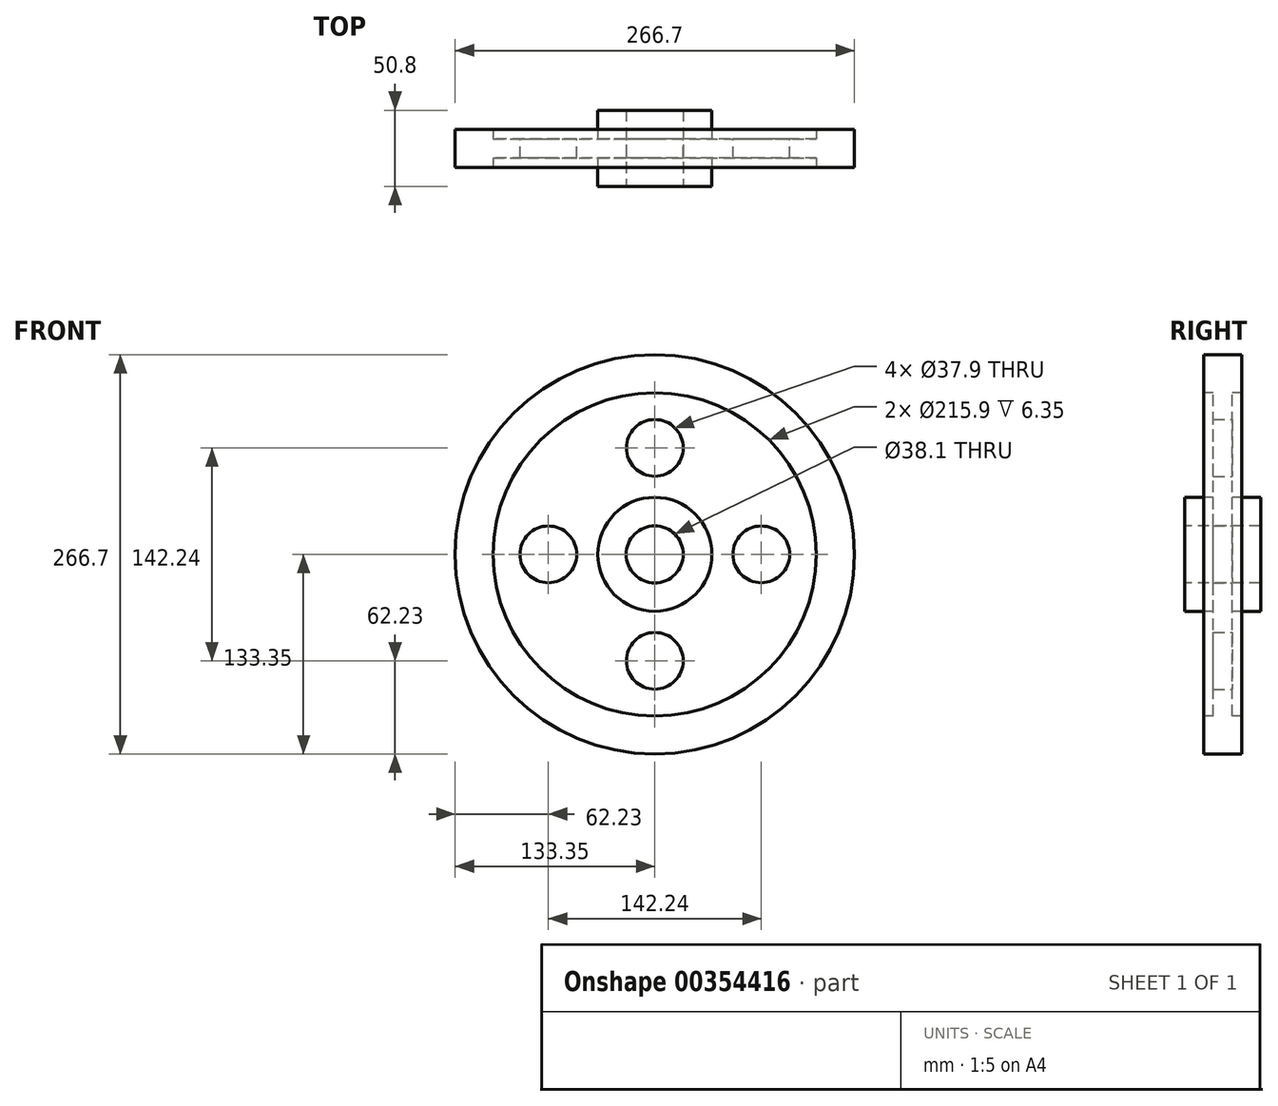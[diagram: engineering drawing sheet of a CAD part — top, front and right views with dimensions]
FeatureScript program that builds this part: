
annotation { "Feature Type Name" : "Feature", "Feature Type Description" : "" }
export const myFeature = defineFeature(function(context is Context, id is Id, definition is map)
    precondition{}
    {
        {
            var Q0;
            Q0=qCreatedBy(makeId("Right.planeOp"),FACE);
            var sketch = newSketch(context, id + "F0", { "sketchPlane" : qUnion([Q0])});
            skLineSegment(sketch, "E0", {"start": v(0, 0) * mm, "end": v(0, 28.58) * mm});
            skLineSegment(sketch, "E1", {"start": v(0, 28.58) * mm, "end": v(0, 73.03) * mm});
            skLineSegment(sketch, "E2", {"start": v(0, 73.03) * mm, "end": v(0, 120.65) * mm});
            skLineSegment(sketch, "E3.bottom", {"start": v(25.4, 19.05) * mm, "end": v(-25.4, 19.05) * mm});
            skLineSegment(sketch, "E3.top", {"start": v(25.4, 38.1) * mm, "end": v(6.35, 38.1) * mm});
            skLineSegment(sketch, "E3.left", {"start": v(25.4, 19.05) * mm, "end": v(25.4, 38.1) * mm});
            skLineSegment(sketch, "E3.right", {"start": v(-25.4, 19.05) * mm, "end": v(-25.4, 38.1) * mm});
            skPoint(sketch, "E3.middle", {"position": v(0, 28.58) * mm});
            skLineSegment(sketch, "E4.bottom", {"start": v(12.7, 107.95) * mm, "end": v(6.35, 107.95) * mm});
            skLineSegment(sketch, "E4.left", {"start": v(12.7, 107.95) * mm, "end": v(12.7, 133.35) * mm});
            skLineSegment(sketch, "E4.right", {"start": v(-12.7, 107.95) * mm, "end": v(-12.7, 133.35) * mm});
            skPoint(sketch, "E4.middle", {"position": v(0, 120.65) * mm});
            skLineSegment(sketch, "E5.top", {"start": v(0, 113.04) * mm, "end": v(-6.35, 113.04) * mm});
            skLineSegment(sketch, "E5.left", {"start": v(6.35, 33.01) * mm, "end": v(6.35, 113.04) * mm});
            skLineSegment(sketch, "E5.right", {"start": v(-6.35, 33.01) * mm, "end": v(-6.35, 113.04) * mm});
            skPoint(sketch, "E5.middle", {"position": v(0, 73.03) * mm});
            skLineSegment(sketch, "E6.trimOffspring", {"start": v(-6.35, 107.95) * mm, "end": v(-12.7, 107.95) * mm});
            skLineSegment(sketch, "E7.trimOffspring", {"start": v(-6.35, 38.1) * mm, "end": v(-25.4, 38.1) * mm});
            skLineSegment(sketch, "E8", {"start": v(0, 0) * mm, "end": v(43.33, 0) * mm});
            skLineSegment(sketch, "E9", {"start": v(-12.7, 133.35) * mm, "end": v(12.7, 133.35) * mm});
            skSolve(sketch);
        }
        {
            var Q0;
            {var subQ4=sQuery(id+"F0.wireOp",EDGE,"E1");Q0=makeQuery(id+"F0.imprint","IMPRINT",FACE,{"disambiguationData":[TD([[makeQuery(id+"F0.imprint","IMPRINT",EDGE,{"derivedFrom":subQ4}),-1.0]])]});}
            var Q1;
            {var subQ5=sQuery(id+"F0.wireOp",EDGE,"E1");Q1=makeQuery(id+"F0.imprint","IMPRINT",FACE,{"disambiguationData":[TD([[makeQuery(id+"F0.imprint","IMPRINT",EDGE,{"derivedFrom":subQ5}),1.0]])]});}
            var Q2;
            Q2=sQuery(id+"F0.wireOp",EDGE,"E8");
            revolve(context, id + "F1", {"entities" : qUnion([Q0, Q1]), "axis" : qUnion([Q2]), "revolveType" : RevolveType.FULL});
        }
        {
            var Q0;
            Q0=makeQuery(id+"F1.opRevolve","SWEPT_FACE",FACE,{"disambiguationData":[OSD([sQuery(id+"F0.wireOp",EDGE,"E5.left")])]});
            var sketch = newSketch(context, id + "F2", { "sketchPlane" : qUnion([Q0])});
            skLineSegment(sketch, "E10", {"start": v(0, 0) * mm, "end": v(0, 71.12) * mm});
            skCircle(sketch, "E11", {"center": v(0, 71.12) * mm, "radius": 18.95 * mm});
            skCircle(sketch, "E12.1.0", {"center": v(-71.12, 0) * mm, "radius": 18.95 * mm});
            skCircle(sketch, "E12.2.0", {"center": v(0, -71.12) * mm, "radius": 18.95 * mm});
            skCircle(sketch, "E12.3.0", {"center": v(71.12, 0) * mm, "radius": 18.95 * mm});
            skPoint(sketch, "E12.center", {"position": v(0, 0) * mm});
            skSolve(sketch);
        }
        {
            var Q0;
            Q0=makeQuery(id+"F2.imprint","IMPRINT",FACE,{"disambiguationData":[TD([[makeQuery(id+"F2.imprint","IMPRINT",EDGE,{"derivedFrom":sQuery(id+"F2.wireOp",EDGE,"E12.3.0")}),1.0]])]});
            var Q1;
            Q1=makeQuery(id+"F2.imprint","IMPRINT",FACE,{"disambiguationData":[TD([[makeQuery(id+"F2.imprint","IMPRINT",EDGE,{"derivedFrom":sQuery(id+"F2.wireOp",EDGE,"E12.2.0")}),1.0]])]});
            var Q2;
            Q2=makeQuery(id+"F2.imprint","IMPRINT",FACE,{"disambiguationData":[TD([[makeQuery(id+"F2.imprint","IMPRINT",EDGE,{"derivedFrom":sQuery(id+"F2.wireOp",EDGE,"E12.1.0")}),1.0]])]});
            var Q3;
            Q3=makeQuery(id+"F2.imprint","IMPRINT",FACE,{"disambiguationData":[TD([[makeQuery(id+"F2.imprint","IMPRINT",EDGE,{"derivedFrom":sQuery(id+"F2.wireOp",EDGE,"E11")}),1.0]])]});
            extrude(context, id + "F3", {"entities" : qUnion([Q0, Q1, Q2, Q3]), "operationType" : NewBodyOperationType.REMOVE, "oppositeDirection" : true, "depth" : 25.4 * mm});
        }
    });
